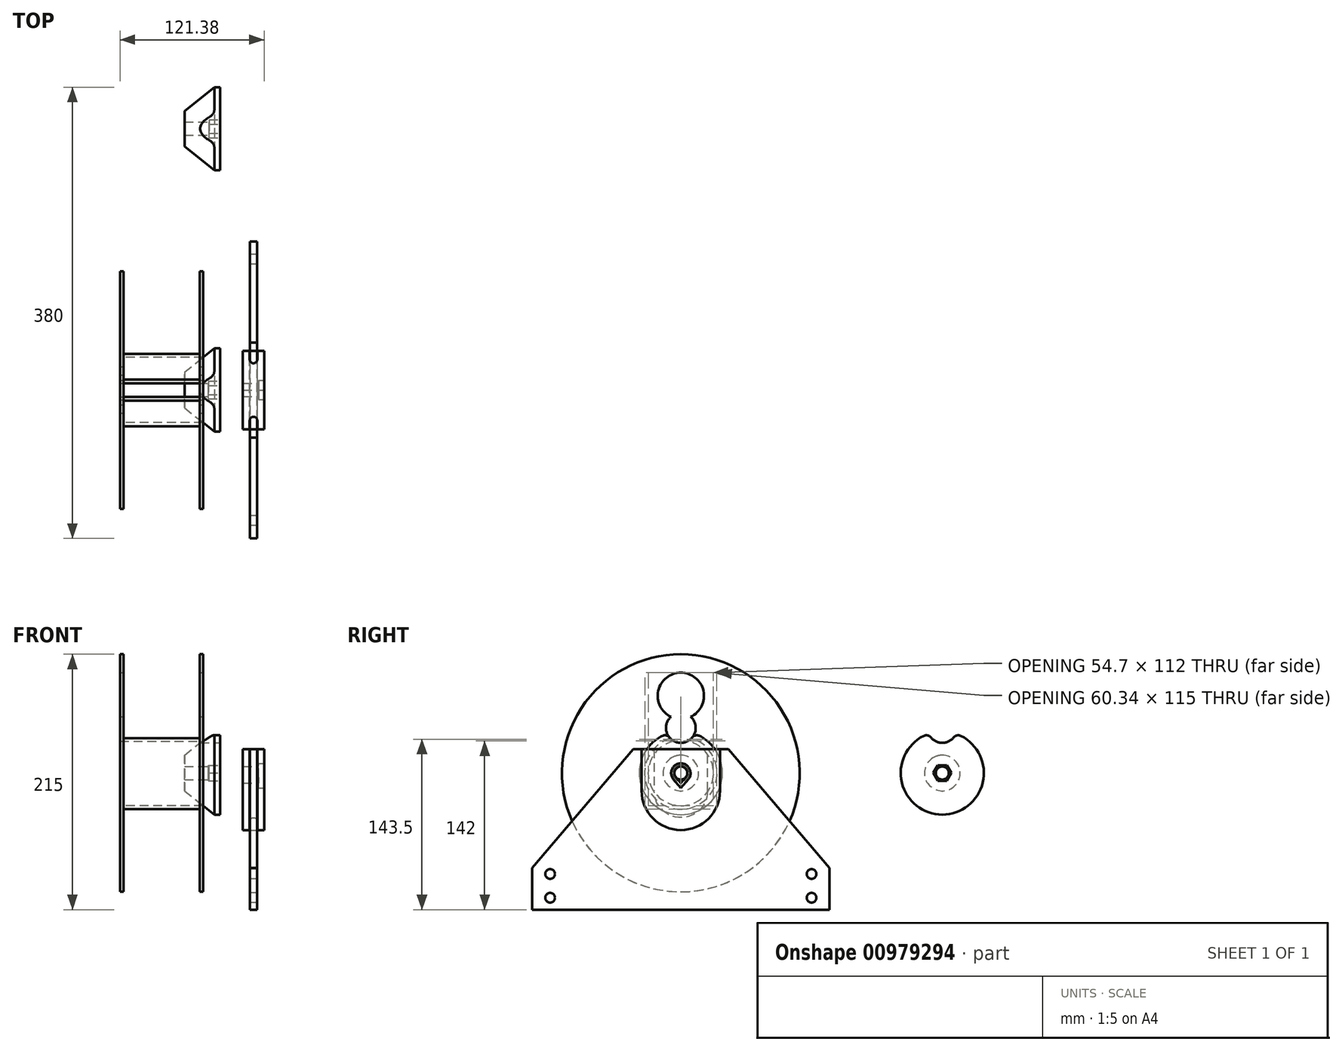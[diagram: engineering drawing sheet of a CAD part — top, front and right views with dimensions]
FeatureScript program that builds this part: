
annotation { "Feature Type Name" : "Feature", "Feature Type Description" : "" }
export const myFeature = defineFeature(function(context is Context, id is Id, definition is map)
    precondition{}
    {
        {
            var Q0;
            Q0=qCreatedBy(makeId("Front.planeOp"),FACE);
            var sketch = newSketch(context, id + "F0", { "sketchPlane" : qUnion([Q0])});
            skLineSegment(sketch, "E0", {"start": v(-35, 100) * mm, "end": v(-35, 27.5) * mm});
            skLineSegment(sketch, "E1", {"start": v(-35, 27.5) * mm, "end": v(35, 27.5) * mm});
            skLineSegment(sketch, "E2", {"start": v(35, 27.5) * mm, "end": v(35, 100) * mm});
            skLineSegment(sketch, "E3", {"start": v(35, 100) * mm, "end": v(32, 100) * mm});
            skLineSegment(sketch, "E4", {"start": v(32, 100) * mm, "end": v(32, 30.5) * mm});
            skLineSegment(sketch, "E5", {"start": v(32, 30.5) * mm, "end": v(-32, 30.5) * mm});
            skLineSegment(sketch, "E6", {"start": v(-32, 30.5) * mm, "end": v(-32, 100) * mm});
            skLineSegment(sketch, "E7", {"start": v(-32, 100) * mm, "end": v(-35, 100) * mm});
            skLineSegment(sketch, "E8", {"start": v(-95.65, 0) * mm, "end": v(81.07, 0) * mm, "construction": true});
            skLineSegment(sketch, "E9", {"start": v(0, 27.5) * mm, "end": v(0, 0) * mm, "construction": true});
            skSolve(sketch);
        }
        {
            var Q0;
            Q0=makeQuery(id+"F0.imprint","IMPRINT",FACE,{"disambiguationData":[TD([[makeQuery(id+"F0.imprint","IMPRINT",EDGE,{"derivedFrom":sQuery(id+"F0.wireOp",EDGE,"E0")}),1.0]])]});
            var Q1;
            Q1=sQuery(id+"F0.wireOp",EDGE,"E8");
            revolve(context, id + "F1", {"surfaceOperationType" : NewSurfaceOperationType.NEW, "entities" : qUnion([Q0]), "axis" : qUnion([Q1]), "revolveType" : RevolveType.FULL});
        }
        {
            var Q0;
            Q0=makeQuery(id+"F1.opRevolve","SWEPT_FACE",FACE,{"disambiguationData":[OSD([sQuery(id+"F0.wireOp",EDGE,"E2")])]});
            var sketch = newSketch(context, id + "F2", { "sketchPlane" : qUnion([Q0])});
            skCircle(sketch, "E10", {"center": v(0, 65) * mm, "radius": 19.5 * mm});
            skSolve(sketch);
        }
        {
            var Q0;
            Q0=makeQuery(id+"F2.imprint","IMPRINT",FACE,{"disambiguationData":[TD([[makeQuery(id+"F2.imprint","IMPRINT",EDGE,{"derivedFrom":sQuery(id+"F2.wireOp",EDGE,"E10")}),1.0]])]});
            extrude(context, id + "F3", {"entities" : qUnion([Q0]), "operationType" : NewBodyOperationType.REMOVE, "endBound" : BoundingType.THROUGH_ALL, "oppositeDirection" : true, "depth" : 25 * mm, "offsetDistance" : 25 * mm});
        }
        {
            var Q0;
            Q0=qCreatedBy(makeId("Front.planeOp"),FACE);
            var sketch = newSketch(context, id + "F4", { "sketchPlane" : qUnion([Q0])});
            skLineSegment(sketch, "E11", {"start": v(12.06, 0) * mm, "end": v(93.62, 0) * mm, "construction": true});
            skLineSegment(sketch, "E12", {"start": v(-35, 27.5) * mm, "end": v(35, 27.5) * mm, "construction": true});
            skLineSegment(sketch, "E13", {"start": v(35, -27.5) * mm, "end": v(-35, -27.5) * mm, "construction": true});
            skLineSegment(sketch, "E14", {"start": v(19.37, 4.1) * mm, "end": v(49.37, 4.1) * mm});
            skLineSegment(sketch, "E15", {"start": v(49.37, 4.1) * mm, "end": v(49.37, 35) * mm});
            skLineSegment(sketch, "E16", {"start": v(49.37, 35) * mm, "end": v(44.37, 35) * mm});
            skLineSegment(sketch, "E17", {"start": v(44.37, 35) * mm, "end": v(19.37, 15) * mm});
            skLineSegment(sketch, "E18", {"start": v(19.37, 15) * mm, "end": v(19.37, 4.1) * mm});
            skSolve(sketch);
        }
        {
            var Q0;
            Q0 = qSketchRegion(id + "F4", true);
            var Q1;
            Q1=sQuery(id+"F4.wireOp",EDGE,"E11");
            revolve(context, id + "F5", {"surfaceOperationType" : NewSurfaceOperationType.NEW, "entities" : qUnion([Q0]), "axis" : qUnion([Q1]), "revolveType" : RevolveType.FULL});
        }
        {
            var Q0;
            Q0=makeQuery(id+"F5.opRevolve","SWEPT_FACE",FACE,{"disambiguationData":[OSD([sQuery(id+"F4.wireOp",EDGE,"E15")])]});
            var sketch = newSketch(context, id + "F6", { "sketchPlane" : qUnion([Q0])});
            skCircle(sketch, "E19", {"center": v(0, 38) * mm, "radius": 12.5 * mm});
            skSolve(sketch);
        }
        {
            var Q0;
            Q0 = qSketchRegion(id + "F6", true);
            extrude(context, id + "F7", {"entities" : qUnion([Q0]), "operationType" : NewBodyOperationType.REMOVE, "endBound" : BoundingType.THROUGH_ALL, "oppositeDirection" : true, "depth" : 25 * mm, "offsetDistance" : 25 * mm});
        }
        {
            var Q0;
            Q0=makeQuery(id+"F7.boolean.opBoolean","INTERSECT",EDGE,{"disambiguationData":[OD(1.0)],"derivedFrom":[makeQuery(id+"F5.opRevolve","SWEPT_FACE",FACE,{"disambiguationData":[OSD([sQuery(id+"F4.wireOp",EDGE,"E16")])]}),makeQuery(id+"F7.opExtrude","SWEPT_FACE",FACE,{"disambiguationData":[OSD([sQuery(id+"F6.wireOp",EDGE,"E19")])]})]});
            var Q1;
            Q1=makeQuery(id+"F7.boolean.opBoolean","INTERSECT",EDGE,{"disambiguationData":[OD(0.0)],"derivedFrom":[makeQuery(id+"F5.opRevolve","SWEPT_FACE",FACE,{"disambiguationData":[OSD([sQuery(id+"F4.wireOp",EDGE,"E16")])]}),makeQuery(id+"F7.opExtrude","SWEPT_FACE",FACE,{"disambiguationData":[OSD([sQuery(id+"F6.wireOp",EDGE,"E19")])]})]});
            fillet(context, id + "F8", {"entities" : qUnion([Q0, Q1]), "radius" : 5 * mm, "tangentPropagation" : true, "allowEdgeOverflow" : false});
        }
        {
            var Q0;
            Q0=makeQuery(id+"F5.opRevolve","SWEPT_FACE",FACE,{"disambiguationData":[OSD([sQuery(id+"F4.wireOp",EDGE,"E15")])]});
            var sketch = newSketch(context, id + "F9", { "sketchPlane" : qUnion([Q0])});
            skCircle(sketch, "E20.cCircle", {"center": v(0, 0) * mm, "radius": 6.55 * mm, "construction": true});
            skLineSegment(sketch, "E20.0", {"start": v(-3.78, 6.55) * mm, "end": v(3.78, 6.55) * mm});
            skLineSegment(sketch, "E20.1", {"start": v(3.78, 6.55) * mm, "end": v(7.56, 0) * mm});
            skLineSegment(sketch, "E20.2", {"start": v(7.56, 0) * mm, "end": v(3.78, -6.55) * mm});
            skLineSegment(sketch, "E20.3", {"start": v(3.78, -6.55) * mm, "end": v(-3.78, -6.55) * mm});
            skLineSegment(sketch, "E20.4", {"start": v(-3.78, -6.55) * mm, "end": v(-7.56, 0) * mm});
            skLineSegment(sketch, "E20.5", {"start": v(-7.56, 0) * mm, "end": v(-3.78, 6.55) * mm});
            skPoint(sketch, "E20.0.midPoint", {"position": v(0, 6.55) * mm});
            skSolve(sketch);
        }
        {
            var Q0;
            Q0 = qSketchRegion(id + "F9", true);
            extrude(context, id + "F10", {"entities" : qUnion([Q0]), "operationType" : NewBodyOperationType.REMOVE, "oppositeDirection" : true, "depth" : 10 * mm, "offsetDistance" : 25 * mm});
        }
        {
            var Q0;
            Q0=makeQuery(id+"F5.opRevolve","SWEPT_BODY",BODY,{"disambiguationData":[OSD([sQuery(id+"F4.wireOp",EDGE,"E14"),sQuery(id+"F4.wireOp",EDGE,"E15"),sQuery(id+"F4.wireOp",EDGE,"E16"),sQuery(id+"F4.wireOp",EDGE,"E17"),sQuery(id+"F4.wireOp",EDGE,"E18")])]});
            transform(context, id + "F11", {"entities" : qUnion([Q0]), "transformType" : TransformType.TRANSLATION_3D, "dx" : 0 * mm, "dy" : 0 * mm, "dz" : 0 * mm, "makeCopy" : true});
        }
        {
            var Q0;
            Q0=makeQuery(id+"F11.opPattern","COPY",BODY,{"derivedFrom":makeQuery(id+"F5.opRevolve","SWEPT_BODY",BODY,{"disambiguationData":[OSD([sQuery(id+"F4.wireOp",EDGE,"E14"),sQuery(id+"F4.wireOp",EDGE,"E15"),sQuery(id+"F4.wireOp",EDGE,"E16"),sQuery(id+"F4.wireOp",EDGE,"E17"),sQuery(id+"F4.wireOp",EDGE,"E18")])]}),"instanceName":"1"});
            deleteBodies(context, id + "F12", {"entities" : qUnion([Q0])});
        }
        {
            var Q0;
            Q0=makeQuery(id+"F5.opRevolve","SWEPT_FACE",FACE,{"disambiguationData":[OSD([sQuery(id+"F4.wireOp",EDGE,"E15")])]});
            cPlane(context, id + "F13", {"entities" : qUnion([Q0]), "cplaneType" : CPlaneType.OFFSET, "offset" : 25 * mm, "width" : 150 * mm, "height" : 150 * mm});
        }
        {
            var Q0;
            Q0=qCreatedBy(id+"F13.planeOp",FACE);
            var sketch = newSketch(context, id + "F14", { "sketchPlane" : qUnion([Q0])});
            skLineSegment(sketch, "E21", {"start": v(-125, -115) * mm, "end": v(-125, -80) * mm});
            skLineSegment(sketch, "E22", {"start": v(-125, -80) * mm, "end": v(-40, 20) * mm});
            skLineSegment(sketch, "E23", {"start": v(-40, 20) * mm, "end": v(-25, 20) * mm});
            skLineSegment(sketch, "E24", {"start": v(-25, 20) * mm, "end": v(-25, -15) * mm});
            skLineSegment(sketch, "E25", {"start": v(-25, -15) * mm, "end": v(25, -15) * mm, "construction": true});
            skLineSegment(sketch, "E26", {"start": v(25, -15) * mm, "end": v(25, 20) * mm});
            skLineSegment(sketch, "E27", {"start": v(25, 20) * mm, "end": v(40, 20) * mm});
            skLineSegment(sketch, "E28", {"start": v(40, 20) * mm, "end": v(125, -80) * mm});
            skLineSegment(sketch, "E29", {"start": v(125, -80) * mm, "end": v(125, -115) * mm});
            skLineSegment(sketch, "E30", {"start": v(125, -115) * mm, "end": v(-125, -115) * mm});
            skLineSegment(sketch, "E31", {"start": v(0, -115) * mm, "end": v(0, 0) * mm, "construction": true});
            skArc(sketch, "E32", {"start": v(-25, -15) * mm, "mid": v(0, -40) * mm, "end": v(25, -15) * mm});
            skCircle(sketch, "E33", {"center": v(-110, -85) * mm, "radius": 4.1 * mm});
            skCircle(sketch, "E34", {"center": v(-110, -105) * mm, "radius": 4.1 * mm});
            skCircle(sketch, "E35", {"center": v(110, -85) * mm, "radius": 4.1 * mm});
            skCircle(sketch, "E36", {"center": v(110, -105) * mm, "radius": 4.1 * mm});
            skLineSegment(sketch, "E37", {"start": v(-110, -85) * mm, "end": v(110, -85) * mm, "construction": true});
            skLineSegment(sketch, "E38", {"start": v(110, -85) * mm, "end": v(110, -105) * mm, "construction": true});
            skLineSegment(sketch, "E39", {"start": v(110, -105) * mm, "end": v(-110, -105) * mm, "construction": true});
            skLineSegment(sketch, "E40", {"start": v(-110, -105) * mm, "end": v(-110, -85) * mm, "construction": true});
            skSolve(sketch);
        }
        {
            var Q0;
            Q0=makeQuery(id+"F14.imprint","IMPRINT",FACE,{"disambiguationData":[TD([[makeQuery(id+"F14.imprint","IMPRINT",EDGE,{"derivedFrom":sQuery(id+"F14.wireOp",EDGE,"E21")}),-1.0]])]});
            extrude(context, id + "F15", {"entities" : qUnion([Q0]), "depth" : 6 * mm, "offsetDistance" : 25 * mm});
        }
        {
            var Q0;
            Q0=makeQuery(id+"F15.opExtrude","CAP_FACE",FACE,{"disambiguationData":[OSD([sQuery(id+"F14.wireOp",EDGE,"E21"),sQuery(id+"F14.wireOp",EDGE,"E22"),sQuery(id+"F14.wireOp",EDGE,"E23"),sQuery(id+"F14.wireOp",EDGE,"E24"),sQuery(id+"F14.wireOp",EDGE,"E26"),sQuery(id+"F14.wireOp",EDGE,"E27"),sQuery(id+"F14.wireOp",EDGE,"E28"),sQuery(id+"F14.wireOp",EDGE,"E29"),sQuery(id+"F14.wireOp",EDGE,"E30"),sQuery(id+"F14.wireOp",EDGE,"E32"),sQuery(id+"F14.wireOp",EDGE,"E33"),sQuery(id+"F14.wireOp",EDGE,"E34"),sQuery(id+"F14.wireOp",EDGE,"E35"),sQuery(id+"F14.wireOp",EDGE,"E36")])],"isStart":false});
            cPlane(context, id + "F16", {"entities" : qUnion([Q0]), "cplaneType" : CPlaneType.OFFSET, "offset" : 3 * mm, "oppositeDirection" : true, "width" : 150 * mm, "height" : 150 * mm});
        }
        {
            var Q0;
            Q0=qCreatedBy(id+"F16.planeOp",FACE);
            var sketch = newSketch(context, id + "F17", { "sketchPlane" : qUnion([Q0])});
            skLineSegment(sketch, "E41.0", {"start": v(-25, 20) * mm, "end": v(-25, -15) * mm});
            skArc(sketch, "E42.0", {"start": v(-25, -15) * mm, "mid": v(0, -40) * mm, "end": v(25, -15) * mm});
            skLineSegment(sketch, "E43.0", {"start": v(25, -15) * mm, "end": v(25, 20) * mm});
            skLineSegment(sketch, "E44.0", {"start": v(33, -15) * mm, "end": v(33, 20) * mm});
            skArc(sketch, "E44.1", {"start": v(-33, -15) * mm, "mid": v(0, -48) * mm, "end": v(33, -15) * mm});
            skLineSegment(sketch, "E44.2", {"start": v(-33, 20) * mm, "end": v(-33, -15) * mm});
            skLineSegment(sketch, "E45", {"start": v(-33, 20) * mm, "end": v(33, 20) * mm});
            skSolve(sketch);
        }
        {
            var Q0;
            {var subQ2=sQuery(id+"F17.wireOp",EDGE,"E41.0");Q0=makeQuery(id+"F17.imprint","IMPRINT",FACE,{"disambiguationData":[TD([[makeQuery(id+"F17.imprint","IMPRINT",EDGE,{"derivedFrom":subQ2}),-1.0]])]});}
            var Q1;
            {var subQ0=sQuery(id+"F17.wireOp",EDGE,"E41.0");Q1=makeQuery(id+"F17.imprint","IMPRINT",FACE,{"disambiguationData":[TD([[makeQuery(id+"F17.imprint","IMPRINT",EDGE,{"derivedFrom":subQ0}),1.0]])]});}
            extrude(context, id + "F18", {"entities" : qUnion([Q0, Q1]), "endBound" : BoundingType.SYMMETRIC, "depth" : 18 * mm, "offsetDistance" : 25 * mm});
        }
        {
            var Q0;
            Q0=makeQuery(id+"F18.opExtrude","SWEPT_FACE",FACE,{"disambiguationData":[OSD([sQuery(id+"F17.wireOp",EDGE,"E45")])]});
            var sketch = newSketch(context, id + "F19", { "sketchPlane" : qUnion([Q0])});
            skLineSegment(sketch, "E46", {"start": v(74.18, -33) * mm, "end": v(74.18, -25.7) * mm});
            skLineSegment(sketch, "E47", {"start": v(74.18, -25.7) * mm, "end": v(80.58, -25.7) * mm, "construction": true});
            skLineSegment(sketch, "E48", {"start": v(80.58, -25.7) * mm, "end": v(80.58, -33) * mm});
            skLineSegment(sketch, "E49", {"start": v(80.58, -33) * mm, "end": v(74.18, -33) * mm});
            skArc(sketch, "E50", {"start": v(74.18, -25.7) * mm, "mid": v(77.38, -22.5) * mm, "end": v(80.58, -25.7) * mm});
            skSolve(sketch);
        }
        {
            var Q0;
            Q0=makeQuery(id+"F19.imprint","IMPRINT",FACE,{"disambiguationData":[TD([[makeQuery(id+"F19.imprint","IMPRINT",EDGE,{"derivedFrom":sQuery(id+"F19.wireOp",EDGE,"E46")}),-1.0]])]});
            var Q1;
            Q1=makeQuery(id+"F18.opExtrude","CAP_EDGE",EDGE,{"disambiguationData":[OSD([sQuery(id+"F17.wireOp",EDGE,"E44.2")])],"isStart":false});
            var Q2;
            Q2=makeQuery(id+"F18.opExtrude","CAP_EDGE",EDGE,{"disambiguationData":[OSD([sQuery(id+"F17.wireOp",EDGE,"E44.1")])],"isStart":false});
            var Q3;
            Q3=makeQuery(id+"F18.opExtrude","CAP_EDGE",EDGE,{"disambiguationData":[OSD([sQuery(id+"F17.wireOp",EDGE,"E44.0")])],"isStart":false});
            sweep(context, id + "F20", {"operationType" : NewBodyOperationType.REMOVE, "profiles" : qUnion([Q0]), "path" : qUnion([Q1, Q2, Q3])});
        }
        {
            var Q0;
            Q0=makeQuery(id+"F18.opExtrude","CAP_FACE",FACE,{"disambiguationData":[OSD([sQuery(id+"F17.wireOp",EDGE,"E44.0"),sQuery(id+"F17.wireOp",EDGE,"E44.1"),sQuery(id+"F17.wireOp",EDGE,"E44.2"),sQuery(id+"F17.wireOp",EDGE,"E45")])],"isStart":false});
            var sketch = newSketch(context, id + "F21", { "sketchPlane" : qUnion([Q0])});
            skCircle(sketch, "E51.0", {"center": v(0, 0) * mm, "radius": 4.1 * mm});
            skCircle(sketch, "E52", {"center": v(0, 0) * mm, "radius": 8.15 * mm});
            skCircle(sketch, "E53.0", {"center": v(0, 0) * mm, "radius": 5.5 * mm});
            skSolve(sketch);
        }
        {
            assignVariable(context, id + "F22", {"variableType" : VariableType.LENGTH, "name" : "Bearings_Depth", "lengthValue" : 4.8 * mm});
        }
        {
            var Q0;
            Q0=makeQuery(id+"F21.imprint","IMPRINT",FACE,{"disambiguationData":[TD([[makeQuery(id+"F21.imprint","IMPRINT",EDGE,{"derivedFrom":sQuery(id+"F21.wireOp",EDGE,"E52")}),1.0]])]});
            var Q1;
            Q1=makeQuery(id+"F21.imprint","IMPRINT",FACE,{"disambiguationData":[TD([[makeQuery(id+"F21.imprint","IMPRINT",EDGE,{"derivedFrom":sQuery(id+"F21.wireOp",EDGE,"E51.0")}),1.0]])]});
            var Q2;
            Q2=makeQuery(id+"F21.imprint","IMPRINT",FACE,{"disambiguationData":[TD([[makeQuery(id+"F21.imprint","IMPRINT",EDGE,{"derivedFrom":sQuery(id+"F21.wireOp",EDGE,"E51.0")}),-1.0]])]});
            extrude(context, id + "F23", {"entities" : qUnion([Q0, Q1, Q2]), "operationType" : NewBodyOperationType.REMOVE, "oppositeDirection" : true, "depth" : getVariable(context, 'Bearings_Depth'), "offsetDistance" : 25 * mm});
        }
        {
            var Q0;
            Q0=makeQuery(id+"F21.imprint","IMPRINT",FACE,{"disambiguationData":[TD([[makeQuery(id+"F21.imprint","IMPRINT",EDGE,{"derivedFrom":sQuery(id+"F21.wireOp",EDGE,"E51.0")}),1.0]])]});
            var Q1;
            Q1=makeQuery(id+"F21.imprint","IMPRINT",FACE,{"disambiguationData":[TD([[makeQuery(id+"F21.imprint","IMPRINT",EDGE,{"derivedFrom":sQuery(id+"F21.wireOp",EDGE,"E51.0")}),-1.0]])]});
            extrude(context, id + "F24", {"entities" : qUnion([Q0, Q1]), "operationType" : NewBodyOperationType.REMOVE, "endBound" : BoundingType.THROUGH_ALL, "oppositeDirection" : true, "depth" : 25 * mm, "offsetDistance" : 25 * mm});
        }
        {
            var Q0;
            Q0=makeQuery(id+"F18.opExtrude","CAP_FACE",FACE,{"disambiguationData":[OSD([sQuery(id+"F17.wireOp",EDGE,"E44.0"),sQuery(id+"F17.wireOp",EDGE,"E44.1"),sQuery(id+"F17.wireOp",EDGE,"E44.2"),sQuery(id+"F17.wireOp",EDGE,"E45")])],"isStart":false});
            var sketch = newSketch(context, id + "F25", { "sketchPlane" : qUnion([Q0])});
            skLineSegment(sketch, "E54", {"start": v(0, 0) * mm, "end": v(0, -29.5) * mm, "construction": true});
            skLineSegment(sketch, "E55", {"start": v(-6.24, -5.24) * mm, "end": v(0, -12.68) * mm});
            skLineSegment(sketch, "E56.MirrorCS", {"start": v(6.24, -5.24) * mm, "end": v(0, -12.68) * mm});
            skSolve(sketch);
        }
        {
            var Q0;
            {var subQ0=sQuery(id+"F25.wireOp",EDGE,"E55");Q0=makeQuery(id+"F25.imprint","IMPRINT",FACE,{"disambiguationData":[TD([[makeQuery(id+"F25.imprint","IMPRINT",EDGE,{"derivedFrom":subQ0}),1.0]])]});}
            var Q1;
            Q1=makeQuery(id+"F23.boolean.opBoolean","COPY",FACE,{"derivedFrom":makeQuery(id+"F23.opExtrude","CAP_FACE",FACE,{"disambiguationData":[OSD([sQuery(id+"F21.wireOp",EDGE,"E52")])],"isStart":false})});
            extrude(context, id + "F26", {"entities" : qUnion([Q0]), "operationType" : NewBodyOperationType.REMOVE, "endBound" : BoundingType.UP_TO_SURFACE, "oppositeDirection" : true, "depth" : 25 * mm, "endBoundEntityFace" : qUnion([Q1]), "offsetDistance" : 25 * mm});
        }
        {
            var Q0;
            {var subQ0=sQuery(id+"F21.wireOp",EDGE,"E52");Q0=makeQuery(id+"F26.boolean.opBoolean","MERGE",FACE,{"derivedFrom":[makeQuery(id+"F23.boolean.opBoolean","COPY",FACE,{"derivedFrom":makeQuery(id+"F23.opExtrude","CAP_FACE",FACE,{"disambiguationData":[OSD([subQ0])],"isStart":false})})],"fromTools":[makeQuery(id+"F26.opExtrude","CAP_FACE",FACE,{"disambiguationData":[OSD([subQ0,sQuery(id+"F25.wireOp",EDGE,"E55"),sQuery(id+"F25.wireOp",EDGE,"E56.MirrorCS")])],"isStart":false})]});}
            var sketch = newSketch(context, id + "F27", { "sketchPlane" : qUnion([Q0])});
            skLineSegment(sketch, "E57", {"start": v(0, 0) * mm, "end": v(0, -10.4) * mm, "construction": true});
            skLineSegment(sketch, "E58", {"start": v(-4.21, -3.54) * mm, "end": v(0, -8.56) * mm});
            skLineSegment(sketch, "E59.MirrorCS", {"start": v(4.21, -3.54) * mm, "end": v(0, -8.56) * mm});
            skSolve(sketch);
        }
        {
            var Q0;
            {var subQ0=sQuery(id+"F27.wireOp",EDGE,"E58");Q0=makeQuery(id+"F27.imprint","IMPRINT",FACE,{"disambiguationData":[TD([[makeQuery(id+"F27.imprint","IMPRINT",EDGE,{"derivedFrom":subQ0}),1.0]])]});}
            extrude(context, id + "F28", {"entities" : qUnion([Q0]), "operationType" : NewBodyOperationType.REMOVE, "endBound" : BoundingType.UP_TO_NEXT, "oppositeDirection" : true, "depth" : 25 * mm, "offsetDistance" : 25 * mm});
        }
        {
            var Q0;
            Q0=makeQuery(id+"F5.opRevolve","SWEPT_BODY",BODY,{"disambiguationData":[OSD([sQuery(id+"F4.wireOp",EDGE,"E14"),sQuery(id+"F4.wireOp",EDGE,"E15"),sQuery(id+"F4.wireOp",EDGE,"E16"),sQuery(id+"F4.wireOp",EDGE,"E17"),sQuery(id+"F4.wireOp",EDGE,"E18")])]});
            transform(context, id + "F29", {"entities" : qUnion([Q0]), "transformType" : TransformType.TRANSLATION_3D, "dx" : 0 * mm, "dy" : 220 * mm, "dz" : 0 * mm, "makeCopy" : true});
        }
        {
            var Q0;
            Q0=makeQuery(id+"F29.opPattern","COPY",FACE,{"derivedFrom":makeQuery(id+"F10.boolean.opBoolean","COPY",FACE,{"derivedFrom":makeQuery(id+"F10.opExtrude","CAP_FACE",FACE,{"disambiguationData":[OSD([sQuery(id+"F9.wireOp",EDGE,"E20.0"),sQuery(id+"F9.wireOp",EDGE,"E20.1"),sQuery(id+"F9.wireOp",EDGE,"E20.2"),sQuery(id+"F9.wireOp",EDGE,"E20.3"),sQuery(id+"F9.wireOp",EDGE,"E20.4"),sQuery(id+"F9.wireOp",EDGE,"E20.5")])],"isStart":false})}),"instanceName":"1"});
            var sketch = newSketch(context, id + "F30", { "sketchPlane" : qUnion([Q0])});
            skLineSegment(sketch, "E60.0.0", {"start": v(216.22, 6.55) * mm, "end": v(212.44, 0) * mm});
            skLineSegment(sketch, "E60.0.1", {"start": v(212.44, 0) * mm, "end": v(216.22, -6.55) * mm});
            skLineSegment(sketch, "E60.0.2", {"start": v(216.22, -6.55) * mm, "end": v(223.78, -6.55) * mm});
            skLineSegment(sketch, "E60.0.3", {"start": v(223.78, -6.55) * mm, "end": v(227.56, 0) * mm});
            skLineSegment(sketch, "E60.0.4", {"start": v(227.56, 0) * mm, "end": v(223.78, 6.55) * mm});
            skLineSegment(sketch, "E60.0.5", {"start": v(223.78, 6.55) * mm, "end": v(216.22, 6.55) * mm});
            skSolve(sketch);
        }
        {
            var Q0;
            Q0=makeQuery(id+"F30.imprint","IMPRINT",FACE,{"disambiguationData":[TD([[makeQuery(id+"F30.imprint","IMPRINT",EDGE,{"derivedFrom":sQuery(id+"F30.wireOp",EDGE,"E60.0.0")}),-1.0]])]});
            var Q1;
            Q1=makeQuery(id+"F30.imprint","IMPRINT",FACE,{"disambiguationData":[TD([[makeQuery(id+"F30.imprint","IMPRINT",EDGE,{"derivedFrom":makeQuery(id+"F29.opPattern","COPY",EDGE,{"derivedFrom":makeQuery(id+"F10.boolean.opBoolean","INTERSECT",EDGE,{"derivedFrom":[makeQuery(id+"F5.opRevolve","SWEPT_FACE",FACE,{"disambiguationData":[OSD([sQuery(id+"F4.wireOp",EDGE,"E14")])]}),makeQuery(id+"F10.opExtrude","CAP_FACE",FACE,{"disambiguationData":[OSD([sQuery(id+"F9.wireOp",EDGE,"E20.0"),sQuery(id+"F9.wireOp",EDGE,"E20.1"),sQuery(id+"F9.wireOp",EDGE,"E20.2"),sQuery(id+"F9.wireOp",EDGE,"E20.3"),sQuery(id+"F9.wireOp",EDGE,"E20.4"),sQuery(id+"F9.wireOp",EDGE,"E20.5")])],"isStart":false})]}),"instanceName":"1"})}),-1.0]])]});
            extrude(context, id + "F31", {"entities" : qUnion([Q0, Q1]), "operationType" : NewBodyOperationType.ADD, "depth" : 0.6 * mm, "offsetDistance" : 25 * mm});
        }
    });
